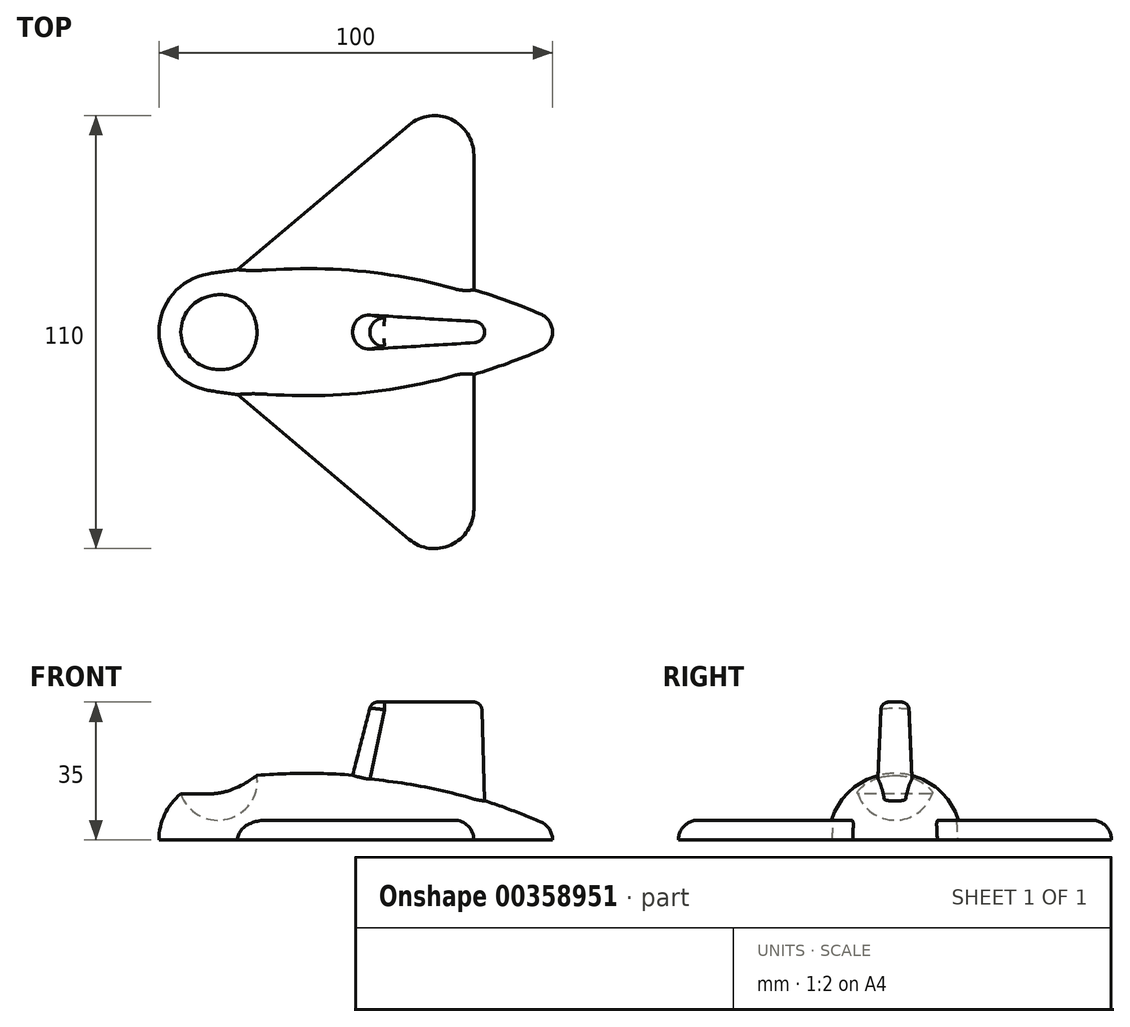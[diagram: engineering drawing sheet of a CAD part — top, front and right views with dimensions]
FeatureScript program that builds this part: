
annotation { "Feature Type Name" : "Feature", "Feature Type Description" : "" }
export const myFeature = defineFeature(function(context is Context, id is Id, definition is map)
    precondition{}
    {
        {
            var Q0;
            Q0=qCreatedBy(makeId("Top.planeOp"),FACE);
            var sketch = newSketch(context, id + "F0", { "sketchPlane" : qUnion([Q0])});
            skArc(sketch, "E0", {"start": v(-2.5, 14.8) * mm, "mid": v(-11.46, 9.68) * mm, "end": v(-15, 0) * mm});
            skArc(sketch, "E1", {"start": v(85, 0) * mm, "mid": v(84.18, 2.75) * mm, "end": v(81.98, 4.6) * mm});
            skLineSegment(sketch, "E2", {"start": v(-15, 0) * mm, "end": v(85, 0) * mm});
            skArc(sketch, "E3", {"start": v(81.98, 4.6) * mm, "mid": v(40.48, 15.8) * mm, "end": v(-2.5, 14.8) * mm});
            skSolve(sketch);
        }
        {
            var Q0;
            Q0 = qSketchRegion(id + "F0", true);
            var Q1;
            Q1=sQuery(id+"F0.wireOp",EDGE,"E2");
            revolve(context, id + "F1", {"entities" : qUnion([Q0]), "axis" : qUnion([Q1]), "revolveType" : RevolveType.ONE_DIRECTION, "angle" : 180 * degree});
        }
        {
            var Q0;
            Q0=qCreatedBy(makeId("Front.planeOp"),FACE);
            var sketch = newSketch(context, id + "F2", { "sketchPlane" : qUnion([Q0])});
            skArc(sketch, "E4", {"start": v(10, 15) * mm, "mid": v(0, 25) * mm, "end": v(-10, 15) * mm});
            skLineSegment(sketch, "E5", {"start": v(10, 15) * mm, "end": v(-10, 15) * mm});
            skPoint(sketch, "E6.orphan", {"position": v(15.15, 15) * mm});
            skSolve(sketch);
        }
        {
            var Q0;
            Q0 = qSketchRegion(id + "F2", true);
            var Q1;
            Q1=sQuery(id+"F2.wireOp",EDGE,"E5");
            revolve(context, id + "F3", {"operationType" : NewBodyOperationType.REMOVE, "entities" : qUnion([Q0]), "axis" : qUnion([Q1]), "revolveType" : RevolveType.FULL, "oppositeDirection" : true});
        }
        {
            var Q0;
            Q0=qCreatedBy(makeId("Top.planeOp"),FACE);
            var sketch = newSketch(context, id + "F4", { "sketchPlane" : qUnion([Q0])});
            skArc(sketch, "E7", {"start": v(35.33, 4.99) * mm, "mid": v(30, 0) * mm, "end": v(35.33, -4.99) * mm});
            skArc(sketch, "E8", {"start": v(65.2, -3) * mm, "mid": v(68, 0) * mm, "end": v(65.2, 3) * mm});
            skLineSegment(sketch, "E9", {"start": v(35.33, -4.99) * mm, "end": v(65.2, -3) * mm});
            skLineSegment(sketch, "E10", {"start": v(35.33, 4.99) * mm, "end": v(65.2, 3) * mm});
            skSolve(sketch);
        }
        {
            var Q0;
            Q0=qCreatedBy(makeId("Top.planeOp"),FACE);
            cPlane(context, id + "F5", {"entities" : qUnion([Q0]), "cplaneType" : CPlaneType.OFFSET, "offset" : 35 * mm, "width" : 150 * mm, "height" : 150 * mm});
        }
        {
            var Q0;
            Q0=qCreatedBy(id+"F5.planeOp",FACE);
            var sketch = newSketch(context, id + "F6", { "sketchPlane" : qUnion([Q0])});
            skArc(sketch, "E11", {"start": v(65.13, -2) * mm, "mid": v(67, 0) * mm, "end": v(65.13, 2) * mm});
            skArc(sketch, "E12", {"start": v(42.73, 3.5) * mm, "mid": v(39, 0) * mm, "end": v(42.73, -3.5) * mm});
            skLineSegment(sketch, "E13", {"start": v(42.73, -3.5) * mm, "end": v(65.13, -2) * mm});
            skLineSegment(sketch, "E14", {"start": v(42.73, 3.5) * mm, "end": v(65.13, 2) * mm});
            skSolve(sketch);
        }
        {
            var Q1;
            Q1=makeQuery(id+"F4.imprint","IMPRINT",FACE,{"disambiguationData":[TD([[makeQuery(id+"F4.imprint","IMPRINT",EDGE,{"derivedFrom":sQuery(id+"F4.wireOp",EDGE,"E7")}),1.0]])]});
            var Q2;
            Q2=makeQuery(id+"F6.imprint","IMPRINT",FACE,{"disambiguationData":[TD([[makeQuery(id+"F6.imprint","IMPRINT",EDGE,{"derivedFrom":sQuery(id+"F6.wireOp",EDGE,"E11")}),1.0]])]});
            loft(context, id + "F7", {"operationType" : NewBodyOperationType.ADD, "sheetProfilesArray" : [{ "sheetProfileEntities" : qUnion([Q1]) }, { "sheetProfileEntities" : qUnion([Q2]) }]});
        }
        {
            var Q0;
            Q0=makeQuery(id+"F7.opLoft","CAP_FACE",FACE,{"disambiguationData":[OSD([makeQuery(id+"F6.imprint","IMPRINT",FACE,{"disambiguationData":[TD([[makeQuery(id+"F6.imprint","IMPRINT",EDGE,{"derivedFrom":sQuery(id+"F6.wireOp",EDGE,"E11")}),1.0]])]})])],"isStart":true});
            fillet(context, id + "F8", {"entities" : qUnion([Q0]), "radius" : 2 * mm, "tangentPropagation" : true, "allowEdgeOverflow" : false});
        }
        {
            var Q0;
            Q0=qCreatedBy(makeId("Top.planeOp"),FACE);
            var sketch = newSketch(context, id + "F9", { "sketchPlane" : qUnion([Q0])});
            skArc(sketch, "E15.0.0", {"start": v(-2.5, -14.8) * mm, "mid": v(-15, 0) * mm, "end": v(-2.5, 14.8) * mm});
            skArc(sketch, "E15.0.1", {"start": v(-2.5, 14.8) * mm, "mid": v(40.48, 15.8) * mm, "end": v(81.98, 4.6) * mm});
            skArc(sketch, "E15.0.2", {"start": v(81.98, 4.6) * mm, "mid": v(85, 0) * mm, "end": v(81.98, -4.6) * mm});
            skArc(sketch, "E15.0.3", {"start": v(81.98, -4.6) * mm, "mid": v(40.48, -15.8) * mm, "end": v(-2.5, -14.8) * mm});
            skLineSegment(sketch, "E16", {"start": v(5, 15.86) * mm, "end": v(48.55, 52.64) * mm});
            skLineSegment(sketch, "E17", {"start": v(65, 45) * mm, "end": v(65, 10.74) * mm});
            skPoint(sketch, "E18.orphan", {"position": v(-13.78, 0) * mm});
            skPoint(sketch, "E19.orphan", {"position": v(65, 0) * mm});
            skPoint(sketch, "E20.visualSharp", {"position": v(65, 66.53) * mm});
            skArc(sketch, "E20.filletArc", {"start": v(65, 45) * mm, "mid": v(59.21, 54.07) * mm, "end": v(48.55, 52.64) * mm});
            skLineSegment(sketch, "E21", {"start": v(5, 15.86) * mm, "end": v(1.7, 13.08) * mm});
            skLineSegment(sketch, "E22", {"start": v(1.7, 13.08) * mm, "end": v(65, 6.23) * mm});
            skLineSegment(sketch, "E23", {"start": v(65, 6.23) * mm, "end": v(65, 10.74) * mm});
            skSolve(sketch);
        }
        {
            var Q0;
            {var subQ0=sQuery(id+"F9.wireOp",EDGE,"E21");Q0=makeQuery(id+"F9.imprint","IMPRINT",FACE,{"disambiguationData":[TD([[makeQuery(id+"F9.imprint","IMPRINT",EDGE,{"derivedFrom":subQ0}),1.0]])]});}
            var Q1;
            {var subQ0=sQuery(id+"F9.wireOp",EDGE,"E16");Q1=makeQuery(id+"F9.imprint","IMPRINT",FACE,{"disambiguationData":[TD([[makeQuery(id+"F9.imprint","IMPRINT",EDGE,{"derivedFrom":subQ0}),-1.0]])]});}
            extrude(context, id + "F10", {"entities" : qUnion([Q0, Q1]), "operationType" : NewBodyOperationType.ADD, "depth" : 5 * mm});
        }
        {
            var Q0;
            Q0=makeQuery(id+"F1.opRevolve","SWEPT_BODY",BODY,{"disambiguationData":[OSD([sQuery(id+"F0.wireOp",EDGE,"E0"),sQuery(id+"F0.wireOp",EDGE,"E1"),sQuery(id+"F0.wireOp",EDGE,"E2"),sQuery(id+"F0.wireOp",EDGE,"E3")])]});
            var Q1;
            Q1=qCreatedBy(makeId("Front.planeOp"),FACE);
            mirror(context, id + "F11", {"operationType" : NewBodyOperationType.ADD, "entities" : qUnion([Q0]), "mirrorPlane" : qUnion([Q1])});
        }
        {
            var Q0;
            Q0=makeQuery(id+"F11.opPattern","COPY",EDGE,{"derivedFrom":makeQuery(id+"F10.opExtrude","CAP_EDGE",EDGE,{"disambiguationData":[OSD([sQuery(id+"F9.wireOp",EDGE,"E20.filletArc")])],"isStart":false}),"instanceName":"1"});
            fillet(context, id + "F12", {"entities" : qUnion([Q0]), "radius" : 5 * mm, "tangentPropagation" : true, "allowEdgeOverflow" : false});
        }
        {
            var Q0;
            Q0=makeQuery(id+"F10.opExtrude","CAP_EDGE",EDGE,{"disambiguationData":[OSD([sQuery(id+"F9.wireOp",EDGE,"E20.filletArc")])],"isStart":false});
            fillet(context, id + "F13", {"entities" : qUnion([Q0]), "radius" : 5 * mm, "tangentPropagation" : true, "allowEdgeOverflow" : false});
        }
    });
